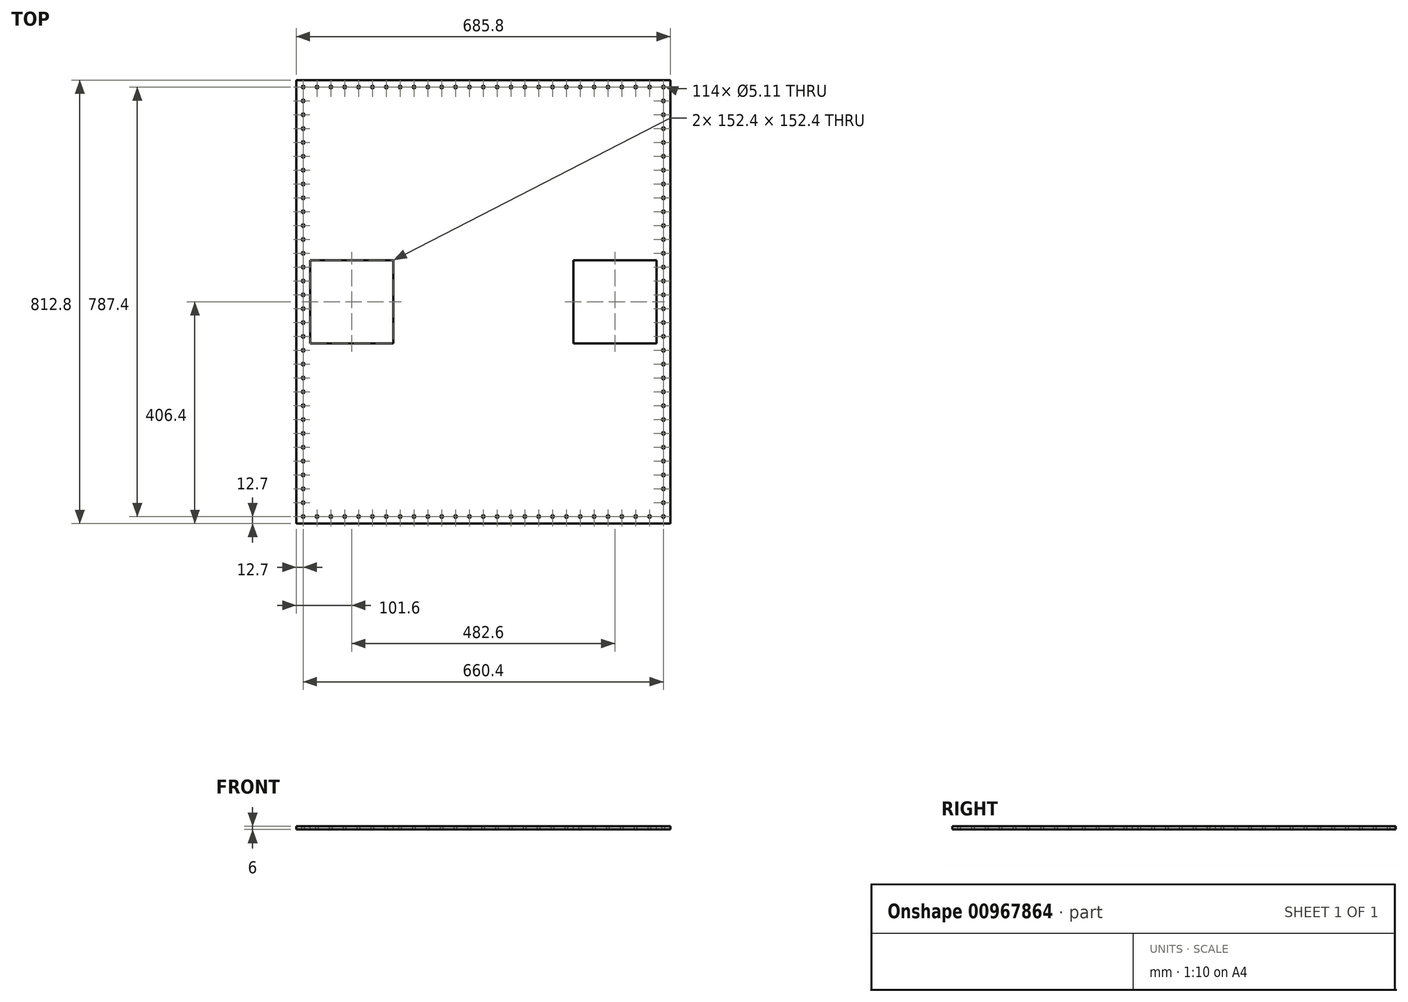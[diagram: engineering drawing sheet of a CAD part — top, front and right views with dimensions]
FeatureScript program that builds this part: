
annotation { "Feature Type Name" : "Feature", "Feature Type Description" : "" }
export const myFeature = defineFeature(function(context is Context, id is Id, definition is map)
    precondition{}
    {
        {
            var Q0;
            Q0=qCreatedBy(makeId("Top.planeOp"),FACE);
            var sketch = newSketch(context, id + "F0", { "sketchPlane" : qUnion([Q0])});
            skLineSegment(sketch, "E0.bottom", {"start": v(342.9, 406.4) * mm, "end": v(-342.9, 406.4) * mm});
            skLineSegment(sketch, "E0.top", {"start": v(342.9, -406.4) * mm, "end": v(-342.9, -406.4) * mm});
            skLineSegment(sketch, "E0.left", {"start": v(342.9, 406.4) * mm, "end": v(342.9, -406.4) * mm});
            skLineSegment(sketch, "E0.right", {"start": v(-342.9, 406.4) * mm, "end": v(-342.9, -406.4) * mm});
            skPoint(sketch, "E0.middle", {"position": v(0, 0) * mm});
            skSolve(sketch);
        }
        {
            var Q0;
            Q0=makeQuery(id+"F0.imprint","IMPRINT",FACE,{"disambiguationData":[TD([[makeQuery(id+"F0.imprint","IMPRINT",EDGE,{"derivedFrom":sQuery(id+"F0.wireOp",EDGE,"E0.bottom")}),1.0]])]});
            extrude(context, id + "F1", {"entities" : qUnion([Q0]), "depth" : 6 * mm, "offsetDistance" : 25.4 * mm});
        }
        {
            var Q0;
            Q0=makeQuery(id+"F1.opExtrude","CAP_FACE",FACE,{"disambiguationData":[OSD([sQuery(id+"F0.wireOp",EDGE,"E0.bottom"),sQuery(id+"F0.wireOp",EDGE,"E0.top"),sQuery(id+"F0.wireOp",EDGE,"E0.left"),sQuery(id+"F0.wireOp",EDGE,"E0.right")])],"isStart":false});
            var sketch = newSketch(context, id + "F2", { "sketchPlane" : qUnion([Q0])});
            skCircle(sketch, "E1", {"center": v(-330.2, 393.7) * mm, "radius": 2.55 * mm});
            skCircle(sketch, "E2.0.1.0", {"center": v(-330.2, 368.3) * mm, "radius": 2.55 * mm});
            skCircle(sketch, "E2.0.2.0", {"center": v(-330.2, 342.9) * mm, "radius": 2.55 * mm});
            skCircle(sketch, "E2.0.3.0", {"center": v(-330.2, 317.5) * mm, "radius": 2.55 * mm});
            skCircle(sketch, "E2.0.4.0", {"center": v(-330.2, 292.1) * mm, "radius": 2.55 * mm});
            skCircle(sketch, "E2.0.5.0", {"center": v(-330.2, 266.7) * mm, "radius": 2.55 * mm});
            skCircle(sketch, "E2.0.6.0", {"center": v(-330.2, 241.3) * mm, "radius": 2.55 * mm});
            skCircle(sketch, "E2.0.7.0", {"center": v(-330.2, 215.9) * mm, "radius": 2.55 * mm});
            skCircle(sketch, "E2.0.8.0", {"center": v(-330.2, 190.5) * mm, "radius": 2.55 * mm});
            skCircle(sketch, "E2.0.9.0", {"center": v(-330.2, 165.1) * mm, "radius": 2.55 * mm});
            skCircle(sketch, "E2.0.10.0", {"center": v(-330.2, 139.7) * mm, "radius": 2.55 * mm});
            skCircle(sketch, "E2.0.11.0", {"center": v(-330.2, 114.3) * mm, "radius": 2.55 * mm});
            skCircle(sketch, "E2.0.12.0", {"center": v(-330.2, 88.9) * mm, "radius": 2.55 * mm});
            skCircle(sketch, "E2.0.13.0", {"center": v(-330.2, 63.5) * mm, "radius": 2.55 * mm});
            skCircle(sketch, "E2.0.14.0", {"center": v(-330.2, 38.1) * mm, "radius": 2.55 * mm});
            skCircle(sketch, "E2.0.15.0", {"center": v(-330.2, 12.7) * mm, "radius": 2.55 * mm});
            skCircle(sketch, "E2.0.16.0", {"center": v(-330.2, -12.7) * mm, "radius": 2.55 * mm});
            skCircle(sketch, "E2.0.17.0", {"center": v(-330.2, -38.1) * mm, "radius": 2.55 * mm});
            skCircle(sketch, "E2.0.18.0", {"center": v(-330.2, -63.5) * mm, "radius": 2.55 * mm});
            skCircle(sketch, "E2.0.19.0", {"center": v(-330.2, -88.9) * mm, "radius": 2.55 * mm});
            skCircle(sketch, "E2.0.20.0", {"center": v(-330.2, -114.3) * mm, "radius": 2.55 * mm});
            skCircle(sketch, "E2.0.21.0", {"center": v(-330.2, -139.7) * mm, "radius": 2.55 * mm});
            skCircle(sketch, "E2.0.22.0", {"center": v(-330.2, -165.1) * mm, "radius": 2.55 * mm});
            skCircle(sketch, "E2.0.23.0", {"center": v(-330.2, -190.5) * mm, "radius": 2.55 * mm});
            skCircle(sketch, "E2.0.24.0", {"center": v(-330.2, -215.9) * mm, "radius": 2.55 * mm});
            skCircle(sketch, "E2.0.25.0", {"center": v(-330.2, -241.3) * mm, "radius": 2.55 * mm});
            skCircle(sketch, "E2.0.26.0", {"center": v(-330.2, -266.7) * mm, "radius": 2.55 * mm});
            skCircle(sketch, "E2.0.27.0", {"center": v(-330.2, -292.1) * mm, "radius": 2.55 * mm});
            skCircle(sketch, "E2.0.28.0", {"center": v(-330.2, -317.5) * mm, "radius": 2.55 * mm});
            skCircle(sketch, "E2.0.29.0", {"center": v(-330.2, -342.9) * mm, "radius": 2.55 * mm});
            skCircle(sketch, "E2.0.30.0", {"center": v(-330.2, -368.3) * mm, "radius": 2.55 * mm});
            skCircle(sketch, "E2.0.31.0", {"center": v(-330.2, -393.7) * mm, "radius": 2.55 * mm});
            skLineSegment(sketch, "E2.direction2", {"start": v(-330.2, 393.7) * mm, "end": v(-330.2, 368.3) * mm, "construction": true});
            skLineSegment(sketch, "E3.direction1", {"start": v(-330.2, -393.7) * mm, "end": v(-304.8, -393.7) * mm, "construction": true});
            skCircle(sketch, "E4.0.1.0", {"center": v(-304.8, -393.7) * mm, "radius": 2.55 * mm});
            skCircle(sketch, "E4.0.2.0", {"center": v(-279.4, -393.7) * mm, "radius": 2.55 * mm});
            skCircle(sketch, "E4.0.3.0", {"center": v(-254, -393.7) * mm, "radius": 2.55 * mm});
            skCircle(sketch, "E4.0.4.0", {"center": v(-228.6, -393.7) * mm, "radius": 2.55 * mm});
            skCircle(sketch, "E4.0.5.0", {"center": v(-203.2, -393.7) * mm, "radius": 2.55 * mm});
            skCircle(sketch, "E4.0.6.0", {"center": v(-177.8, -393.7) * mm, "radius": 2.55 * mm});
            skCircle(sketch, "E4.0.7.0", {"center": v(-152.4, -393.7) * mm, "radius": 2.55 * mm});
            skCircle(sketch, "E4.0.8.0", {"center": v(-127, -393.7) * mm, "radius": 2.55 * mm});
            skCircle(sketch, "E4.0.9.0", {"center": v(-101.6, -393.7) * mm, "radius": 2.55 * mm});
            skCircle(sketch, "E4.0.10.0", {"center": v(-76.2, -393.7) * mm, "radius": 2.55 * mm});
            skCircle(sketch, "E4.0.11.0", {"center": v(-50.8, -393.7) * mm, "radius": 2.55 * mm});
            skCircle(sketch, "E4.0.12.0", {"center": v(-25.4, -393.7) * mm, "radius": 2.55 * mm});
            skCircle(sketch, "E4.0.13.0", {"center": v(0, -393.7) * mm, "radius": 2.55 * mm});
            skCircle(sketch, "E4.0.14.0", {"center": v(25.4, -393.7) * mm, "radius": 2.55 * mm});
            skCircle(sketch, "E4.0.15.0", {"center": v(50.8, -393.7) * mm, "radius": 2.55 * mm});
            skCircle(sketch, "E4.0.16.0", {"center": v(76.2, -393.7) * mm, "radius": 2.55 * mm});
            skCircle(sketch, "E4.0.17.0", {"center": v(101.6, -393.7) * mm, "radius": 2.55 * mm});
            skCircle(sketch, "E4.0.18.0", {"center": v(127, -393.7) * mm, "radius": 2.55 * mm});
            skCircle(sketch, "E4.0.19.0", {"center": v(152.4, -393.7) * mm, "radius": 2.55 * mm});
            skCircle(sketch, "E4.0.20.0", {"center": v(177.8, -393.7) * mm, "radius": 2.55 * mm});
            skCircle(sketch, "E4.0.21.0", {"center": v(203.2, -393.7) * mm, "radius": 2.55 * mm});
            skCircle(sketch, "E4.0.22.0", {"center": v(228.6, -393.7) * mm, "radius": 2.55 * mm});
            skCircle(sketch, "E4.0.23.0", {"center": v(254, -393.7) * mm, "radius": 2.55 * mm});
            skCircle(sketch, "E4.0.24.0", {"center": v(279.4, -393.7) * mm, "radius": 2.55 * mm});
            skCircle(sketch, "E4.0.25.0", {"center": v(304.8, -393.7) * mm, "radius": 2.55 * mm});
            skCircle(sketch, "E4.0.26.0", {"center": v(330.2, -393.7) * mm, "radius": 2.55 * mm});
            skCircle(sketch, "E5.1.0.0", {"center": v(-304.8, 393.7) * mm, "radius": 2.55 * mm});
            skCircle(sketch, "E5.2.0.0", {"center": v(-279.4, 393.7) * mm, "radius": 2.55 * mm});
            skCircle(sketch, "E5.3.0.0", {"center": v(-254, 393.7) * mm, "radius": 2.55 * mm});
            skCircle(sketch, "E5.4.0.0", {"center": v(-228.6, 393.7) * mm, "radius": 2.55 * mm});
            skCircle(sketch, "E5.5.0.0", {"center": v(-203.2, 393.7) * mm, "radius": 2.55 * mm});
            skCircle(sketch, "E5.6.0.0", {"center": v(-177.8, 393.7) * mm, "radius": 2.55 * mm});
            skCircle(sketch, "E5.7.0.0", {"center": v(-152.4, 393.7) * mm, "radius": 2.55 * mm});
            skCircle(sketch, "E5.8.0.0", {"center": v(-127, 393.7) * mm, "radius": 2.55 * mm});
            skCircle(sketch, "E5.9.0.0", {"center": v(-101.6, 393.7) * mm, "radius": 2.55 * mm});
            skCircle(sketch, "E5.10.0.0", {"center": v(-76.2, 393.7) * mm, "radius": 2.55 * mm});
            skCircle(sketch, "E5.11.0.0", {"center": v(-50.8, 393.7) * mm, "radius": 2.55 * mm});
            skCircle(sketch, "E5.12.0.0", {"center": v(-25.4, 393.7) * mm, "radius": 2.55 * mm});
            skCircle(sketch, "E5.13.0.0", {"center": v(0, 393.7) * mm, "radius": 2.55 * mm});
            skCircle(sketch, "E5.14.0.0", {"center": v(25.4, 393.7) * mm, "radius": 2.55 * mm});
            skCircle(sketch, "E5.15.0.0", {"center": v(50.8, 393.7) * mm, "radius": 2.55 * mm});
            skCircle(sketch, "E5.16.0.0", {"center": v(76.2, 393.7) * mm, "radius": 2.55 * mm});
            skCircle(sketch, "E5.17.0.0", {"center": v(101.6, 393.7) * mm, "radius": 2.55 * mm});
            skCircle(sketch, "E5.18.0.0", {"center": v(127, 393.7) * mm, "radius": 2.55 * mm});
            skCircle(sketch, "E5.19.0.0", {"center": v(152.4, 393.7) * mm, "radius": 2.55 * mm});
            skCircle(sketch, "E5.20.0.0", {"center": v(177.8, 393.7) * mm, "radius": 2.55 * mm});
            skCircle(sketch, "E5.21.0.0", {"center": v(203.2, 393.7) * mm, "radius": 2.55 * mm});
            skCircle(sketch, "E5.22.0.0", {"center": v(228.6, 393.7) * mm, "radius": 2.55 * mm});
            skCircle(sketch, "E5.23.0.0", {"center": v(254, 393.7) * mm, "radius": 2.55 * mm});
            skCircle(sketch, "E5.24.0.0", {"center": v(279.4, 393.7) * mm, "radius": 2.55 * mm});
            skCircle(sketch, "E5.25.0.0", {"center": v(304.8, 393.7) * mm, "radius": 2.55 * mm});
            skCircle(sketch, "E5.26.0.0", {"center": v(330.2, 393.7) * mm, "radius": 2.55 * mm});
            skLineSegment(sketch, "E5.direction1", {"start": v(-330.2, 393.7) * mm, "end": v(-304.8, 393.7) * mm, "construction": true});
            skCircle(sketch, "E6.0.1.0", {"center": v(330.2, 368.3) * mm, "radius": 2.55 * mm});
            skCircle(sketch, "E6.0.2.0", {"center": v(330.2, 342.9) * mm, "radius": 2.55 * mm});
            skCircle(sketch, "E6.0.3.0", {"center": v(330.2, 317.5) * mm, "radius": 2.55 * mm});
            skCircle(sketch, "E6.0.4.0", {"center": v(330.2, 292.1) * mm, "radius": 2.55 * mm});
            skCircle(sketch, "E6.0.5.0", {"center": v(330.2, 266.7) * mm, "radius": 2.55 * mm});
            skCircle(sketch, "E6.0.6.0", {"center": v(330.2, 241.3) * mm, "radius": 2.55 * mm});
            skCircle(sketch, "E6.0.7.0", {"center": v(330.2, 215.9) * mm, "radius": 2.55 * mm});
            skCircle(sketch, "E6.0.8.0", {"center": v(330.2, 190.5) * mm, "radius": 2.55 * mm});
            skCircle(sketch, "E6.0.9.0", {"center": v(330.2, 165.1) * mm, "radius": 2.55 * mm});
            skCircle(sketch, "E6.0.10.0", {"center": v(330.2, 139.7) * mm, "radius": 2.55 * mm});
            skCircle(sketch, "E6.0.11.0", {"center": v(330.2, 114.3) * mm, "radius": 2.55 * mm});
            skCircle(sketch, "E6.0.12.0", {"center": v(330.2, 88.9) * mm, "radius": 2.55 * mm});
            skCircle(sketch, "E6.0.13.0", {"center": v(330.2, 63.5) * mm, "radius": 2.55 * mm});
            skCircle(sketch, "E6.0.14.0", {"center": v(330.2, 38.1) * mm, "radius": 2.55 * mm});
            skCircle(sketch, "E6.0.15.0", {"center": v(330.2, 12.7) * mm, "radius": 2.55 * mm});
            skCircle(sketch, "E6.0.16.0", {"center": v(330.2, -12.7) * mm, "radius": 2.55 * mm});
            skCircle(sketch, "E6.0.17.0", {"center": v(330.2, -38.1) * mm, "radius": 2.55 * mm});
            skCircle(sketch, "E6.0.18.0", {"center": v(330.2, -63.5) * mm, "radius": 2.55 * mm});
            skCircle(sketch, "E6.0.19.0", {"center": v(330.2, -88.9) * mm, "radius": 2.55 * mm});
            skCircle(sketch, "E6.0.20.0", {"center": v(330.2, -114.3) * mm, "radius": 2.55 * mm});
            skCircle(sketch, "E6.0.21.0", {"center": v(330.2, -139.7) * mm, "radius": 2.55 * mm});
            skCircle(sketch, "E6.0.22.0", {"center": v(330.2, -165.1) * mm, "radius": 2.55 * mm});
            skCircle(sketch, "E6.0.23.0", {"center": v(330.2, -190.5) * mm, "radius": 2.55 * mm});
            skCircle(sketch, "E6.0.24.0", {"center": v(330.2, -215.9) * mm, "radius": 2.55 * mm});
            skCircle(sketch, "E6.0.25.0", {"center": v(330.2, -241.3) * mm, "radius": 2.55 * mm});
            skCircle(sketch, "E6.0.26.0", {"center": v(330.2, -266.7) * mm, "radius": 2.55 * mm});
            skCircle(sketch, "E6.0.27.0", {"center": v(330.2, -292.1) * mm, "radius": 2.55 * mm});
            skCircle(sketch, "E6.0.28.0", {"center": v(330.2, -317.5) * mm, "radius": 2.55 * mm});
            skCircle(sketch, "E6.0.29.0", {"center": v(330.2, -342.9) * mm, "radius": 2.55 * mm});
            skCircle(sketch, "E6.0.30.0", {"center": v(330.2, -368.3) * mm, "radius": 2.55 * mm});
            skLineSegment(sketch, "E6.direction1", {"start": v(330.2, 393.7) * mm, "end": v(355.6, 393.7) * mm, "construction": true});
            skLineSegment(sketch, "E6.direction2", {"start": v(330.2, 393.7) * mm, "end": v(330.2, 368.3) * mm, "construction": true});
            skSolve(sketch);
        }
        {
            var Q0;
            Q0=qSketchRegion(id+"F2",true);
            extrude(context, id + "F3", {"entities" : qUnion([Q0]), "operationType" : NewBodyOperationType.REMOVE, "oppositeDirection" : true, "depth" : 25.4 * mm, "offsetDistance" : 25.4 * mm});
        }
        {
            var Q0;
            Q0=makeQuery(id+"F1.opExtrude","CAP_FACE",FACE,{"disambiguationData":[OSD([sQuery(id+"F0.wireOp",EDGE,"E0.bottom"),sQuery(id+"F0.wireOp",EDGE,"E0.top"),sQuery(id+"F0.wireOp",EDGE,"E0.left"),sQuery(id+"F0.wireOp",EDGE,"E0.right")])],"isStart":false});
            var sketch = newSketch(context, id + "F4", { "sketchPlane" : qUnion([Q0])});
            skLineSegment(sketch, "E7.bottom", {"start": v(-317.5, 76.2) * mm, "end": v(-165.1, 76.2) * mm});
            skLineSegment(sketch, "E7.top", {"start": v(-317.5, -76.2) * mm, "end": v(-165.1, -76.2) * mm});
            skLineSegment(sketch, "E7.left", {"start": v(-317.5, 76.2) * mm, "end": v(-317.5, -76.2) * mm});
            skLineSegment(sketch, "E7.right", {"start": v(-165.1, 76.2) * mm, "end": v(-165.1, -76.2) * mm});
            skPoint(sketch, "E7.middle", {"position": v(-241.3, 0) * mm});
            skLineSegment(sketch, "E8.bottom", {"start": v(317.5, -76.2) * mm, "end": v(165.1, -76.2) * mm});
            skLineSegment(sketch, "E8.top", {"start": v(317.5, 76.2) * mm, "end": v(165.1, 76.2) * mm});
            skLineSegment(sketch, "E8.left", {"start": v(317.5, -76.2) * mm, "end": v(317.5, 76.2) * mm});
            skLineSegment(sketch, "E8.right", {"start": v(165.1, -76.2) * mm, "end": v(165.1, 76.2) * mm});
            skPoint(sketch, "E8.middle", {"position": v(241.3, 0) * mm});
            skSolve(sketch);
        }
        {
            var Q0;
            Q0=qSketchRegion(id+"F4",true);
            extrude(context, id + "F5", {"entities" : qUnion([Q0]), "operationType" : NewBodyOperationType.REMOVE, "endBound" : BoundingType.THROUGH_ALL, "oppositeDirection" : true, "depth" : 25.4 * mm, "offsetDistance" : 25.4 * mm});
        }
    });
